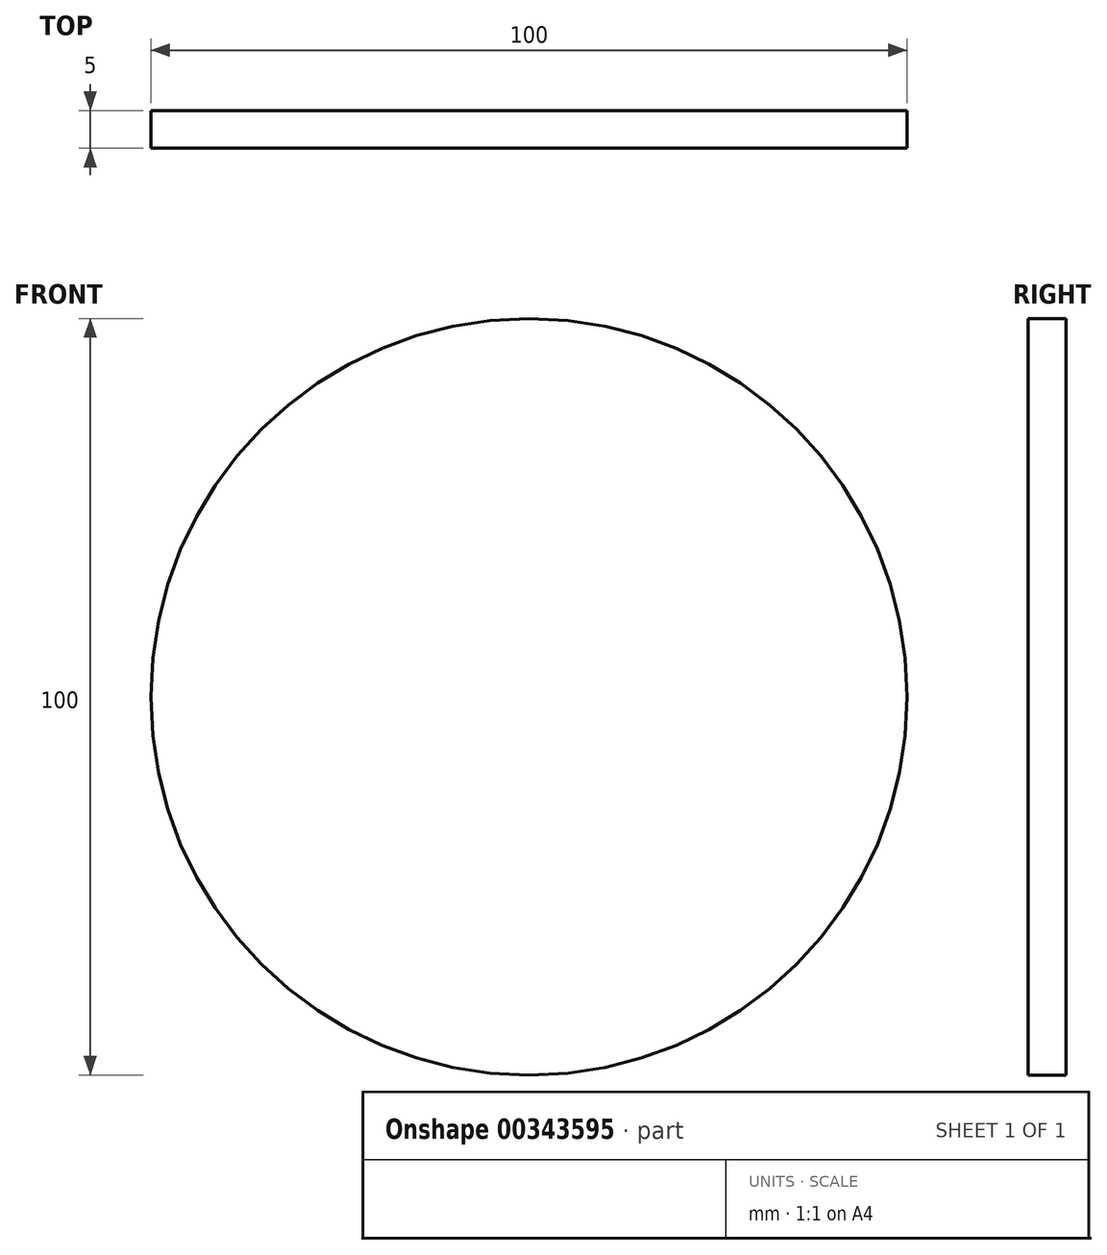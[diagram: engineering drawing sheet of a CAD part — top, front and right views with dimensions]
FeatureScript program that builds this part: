
annotation { "Feature Type Name" : "Feature", "Feature Type Description" : "" }
export const myFeature = defineFeature(function(context is Context, id is Id, definition is map)
    precondition{}
    {
        {
            assignVariable(context, id + "F0", {"name" : "Span", "anyValue" : 5});
        }
        {
            var Q0;
            Q0=qCreatedBy(makeId("Front.planeOp"),FACE);
            var sketch = newSketch(context, id + "F1", { "sketchPlane" : qUnion([Q0])});
            skCircle(sketch, "E0", {"center": v(0, -4.8) * mm, "radius": 50 * mm});
            skSolve(sketch);
        }
        {
            var Q0;
            Q0=makeQuery(id+"F1.imprint","IMPRINT",FACE,{"disambiguationData":[TD([[makeQuery(id+"F1.imprint","IMPRINT",EDGE,{"derivedFrom":sQuery(id+"F1.wireOp",EDGE,"E0")}),1.0]])]});
            extrude(context, id + "F2", {"entities" : qUnion([Q0]), "depth" : (getVariable(context, 'Span')) * mm});
        }
    });
